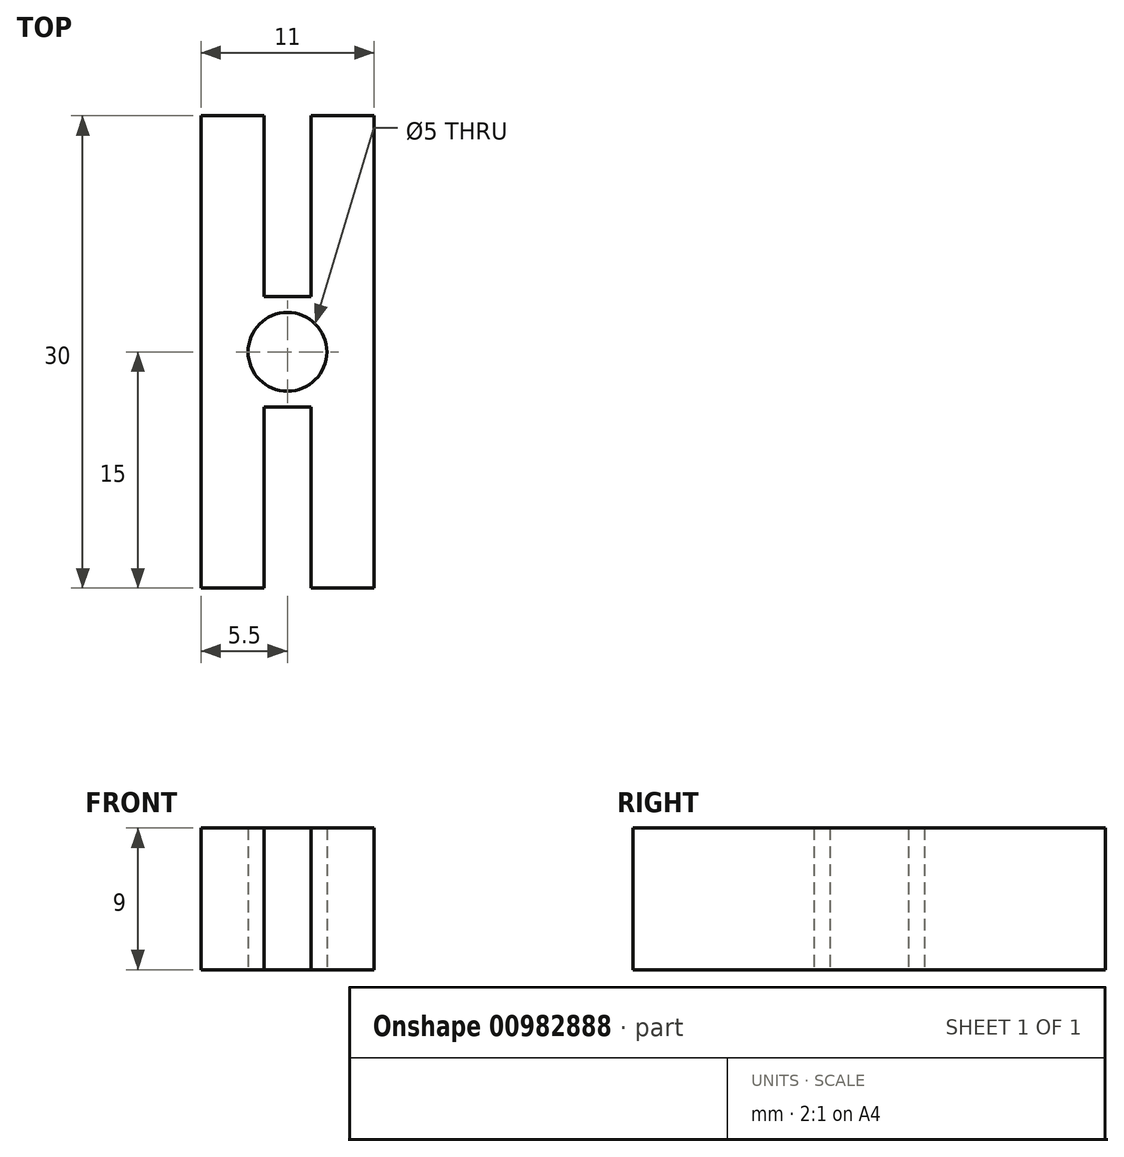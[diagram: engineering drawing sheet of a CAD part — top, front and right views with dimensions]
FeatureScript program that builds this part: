
annotation { "Feature Type Name" : "Feature", "Feature Type Description" : "" }
export const myFeature = defineFeature(function(context is Context, id is Id, definition is map)
    precondition{}
    {
        {
            var Q0;
            Q0=qCreatedBy(makeId("Top.planeOp"),FACE);
            var sketch = newSketch(context, id + "F0", { "sketchPlane" : qUnion([Q0])});
            skLineSegment(sketch, "E0.bottom", {"start": v(5.5, 15) * mm, "end": v(1.5, 15) * mm});
            skLineSegment(sketch, "E0.top", {"start": v(5.5, -15) * mm, "end": v(1.5, -15) * mm});
            skLineSegment(sketch, "E0.left", {"start": v(5.5, 15) * mm, "end": v(5.5, -15) * mm});
            skLineSegment(sketch, "E0.right", {"start": v(-5.5, 15) * mm, "end": v(-5.5, -15) * mm});
            skPoint(sketch, "E0.middle", {"position": v(0, 0) * mm});
            skCircle(sketch, "E1", {"center": v(0, 0) * mm, "radius": 2.5 * mm});
            skLineSegment(sketch, "E2.top", {"start": v(-1.5, 3.5) * mm, "end": v(1.5, 3.5) * mm});
            skLineSegment(sketch, "E2.left", {"start": v(-1.5, 15) * mm, "end": v(-1.5, 3.5) * mm});
            skLineSegment(sketch, "E2.right", {"start": v(1.5, 15) * mm, "end": v(1.5, 3.5) * mm});
            skPoint(sketch, "E3", {"position": v(0, 3.5) * mm});
            skPoint(sketch, "E3.positionSnap0", {"position": v(0, 3.5) * mm});
            skLineSegment(sketch, "E4.MirrorCS", {"start": v(-1.5, -15) * mm, "end": v(-1.5, -3.5) * mm});
            skLineSegment(sketch, "E5.MirrorCS", {"start": v(1.5, -15) * mm, "end": v(1.5, -3.5) * mm});
            skLineSegment(sketch, "E6.MirrorCS", {"start": v(-1.5, -3.5) * mm, "end": v(1.5, -3.5) * mm});
            skLineSegment(sketch, "E7.trimOffspring", {"start": v(-1.5, -15) * mm, "end": v(-5.5, -15) * mm});
            skLineSegment(sketch, "E8.trimOffspring", {"start": v(-1.5, 15) * mm, "end": v(-5.5, 15) * mm});
            skSolve(sketch);
        }
        {
            var Q0;
            Q0 = qSketchRegion(id + "F0", true);
            extrude(context, id + "F1", {"entities" : qUnion([Q0]), "depth" : 9 * mm, "offsetDistance" : 25 * mm});
        }
    });
